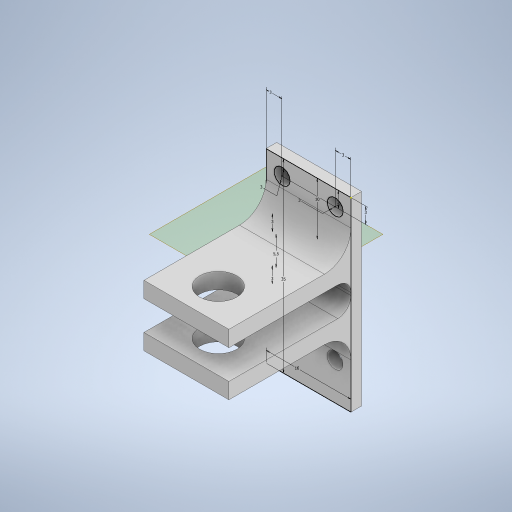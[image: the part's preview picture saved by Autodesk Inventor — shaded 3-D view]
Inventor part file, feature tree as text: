
AUTODESK INVENTOR PART (.ipt)
format: ipt  version: 2024.2 (Build 282272000, 272)  size: 314,368 bytes
history: native  units: mm
features: extrude x5, other x4, sketch x3, fillet x1, projected_geometry x1
ambient origin geometry x8: Origin, YZ Plane, XZ Plane, XY Plane, X Axis, Y Axis, Z Axis, Center Point
bodies: Body1 (feature_tree)
feature tree (14):
  sketch  "Эскиз6"
  extrude  "Выдавливание8"  Depth=16.0mm
  other  "РабПлоскость12"
  sketch  "Эскиз7"
  extrude  "Выдавливание11"  Depth=35.0mm
  extrude  "Выдавливание12"  Depth=3.0mm
  other  "Сопряжение грани1"
  other  "Сопряжение грани2"
  other  "Сопряжение грани3"
  fillet  "Сопряжение1"  Radius=3.0mm
  extrude  "Выдавливание13"  Depth=3.0mm
  extrude  "Выдавливание14"  Depth=3.0mm
  sketch  "Эскиз8"
  projected_geometry  "Спроецированная петля3"
